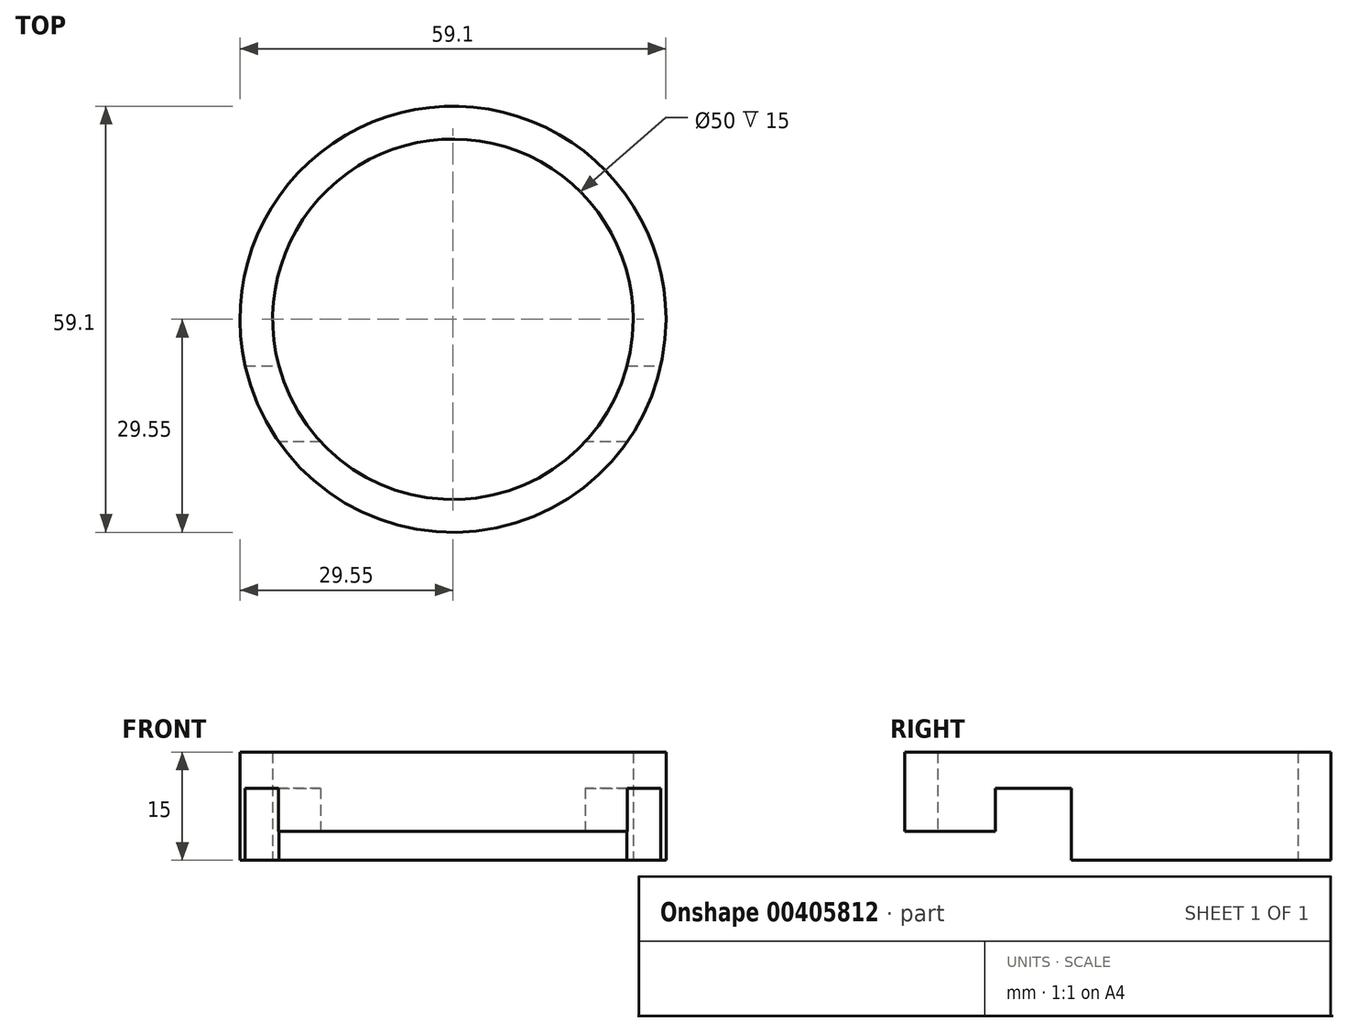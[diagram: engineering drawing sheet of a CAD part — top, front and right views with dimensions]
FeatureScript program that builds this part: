
annotation { "Feature Type Name" : "Feature", "Feature Type Description" : "" }
export const myFeature = defineFeature(function(context is Context, id is Id, definition is map)
    precondition{}
    {
        {
            var Q0;
            Q0=qCreatedBy(makeId("Top.planeOp"),FACE);
            var sketch = newSketch(context, id + "F0", { "sketchPlane" : qUnion([Q0])});
            skCircle(sketch, "E0", {"center": v(0, 0) * mm, "radius": 29.55 * mm});
            skCircle(sketch, "E1", {"center": v(0, 0) * mm, "radius": 25 * mm});
            skSolve(sketch);
        }
        {
            var Q0;
            Q0 = qSketchRegion(id + "F0", true);
            extrude(context, id + "F1", {"entities" : qUnion([Q0]), "depth" : 15 * mm});
        }
        {
            var Q0;
            Q0=qCreatedBy(makeId("Top.planeOp"),FACE);
            var sketch = newSketch(context, id + "F2", { "sketchPlane" : qUnion([Q0])});
            skLineSegment(sketch, "E2", {"start": v(-26.47, -10.46) * mm, "end": v(29.4, -10.46) * mm});
            skLineSegment(sketch, "E3", {"start": v(29.4, -10.46) * mm, "end": v(29.4, -17) * mm});
            skLineSegment(sketch, "E4", {"start": v(29.4, -17) * mm, "end": v(-27.45, -17) * mm});
            skLineSegment(sketch, "E5", {"start": v(-27.45, -17) * mm, "end": v(-26.47, -10.46) * mm});
            skSolve(sketch);
        }
        {
            var Q0;
            Q0 = qSketchRegion(id + "F2", true);
            extrude(context, id + "F3", {"entities" : qUnion([Q0]), "operationType" : NewBodyOperationType.REMOVE, "depth" : 10 * mm});
        }
        {
            var Q0;
            {var subQ0=sQuery(id+"F0.wireOp",EDGE,"E0");var subQ1=sQuery(id+"F0.wireOp",EDGE,"E1");Q0=makeQuery(id+"F3.boolean.opBoolean","SPLIT",FACE,{"disambiguationData":[TD([makeQuery(id+"F3.opExtrude","SWEPT_FACE",FACE,{"disambiguationData":[OSD([sQuery(id+"F2.wireOp",EDGE,"E4")])]})])],"derivedFrom":makeQuery(id+"F1.opExtrude","CAP_FACE",FACE,{"disambiguationData":[OSD([subQ0,subQ1])],"isStart":true})});}
            extrude(context, id + "F4", {"entities" : qUnion([Q0]), "operationType" : NewBodyOperationType.REMOVE, "oppositeDirection" : true, "depth" : 4 * mm});
        }
        {
            var Q0;
            Q0=makeQuery(id+"F3.boolean.opBoolean","COPY",FACE,{"derivedFrom":makeQuery(id+"F3.opExtrude","SWEPT_FACE",FACE,{"disambiguationData":[OSD([sQuery(id+"F2.wireOp",EDGE,"E5")])]})});
            extrude(context, id + "F5", {"entities" : qUnion([Q0]), "operationType" : NewBodyOperationType.REMOVE, "oppositeDirection" : true, "depth" : 25 * mm});
        }
        {
            var Q0;
            {var subQ0=sQuery(id+"F0.wireOp",EDGE,"E0");var subQ1=sQuery(id+"F2.wireOp",EDGE,"E2");Q0=makeQuery(id+"F3.boolean.opBoolean","COPY",FACE,{"disambiguationData":[TD([makeQuery(id+"F1.opExtrude","SWEPT_FACE",FACE,{"disambiguationData":[OSD([subQ0])]})])],"derivedFrom":makeQuery(id+"F3.opExtrude","SWEPT_FACE",FACE,{"disambiguationData":[OSD([subQ1])]})});}
            var Q1;
            {var subQ1=sQuery(id+"F2.wireOp",EDGE,"E5");var subQ2=sQuery(id+"F2.wireOp",EDGE,"E2");Q1=makeQuery(id+"F3.boolean.opBoolean","COPY",FACE,{"disambiguationData":[TD([makeQuery(id+"F3.opExtrude","SWEPT_FACE",FACE,{"disambiguationData":[OSD([subQ1])]})])],"derivedFrom":makeQuery(id+"F3.opExtrude","SWEPT_FACE",FACE,{"disambiguationData":[OSD([subQ2])]})});}
            extrude(context, id + "F6", {"entities" : qUnion([Q0, Q1]), "operationType" : NewBodyOperationType.REMOVE, "oppositeDirection" : true, "depth" : 4 * mm});
        }
        {
            var Q0;
            Q0=makeQuery(id+"F6.boolean.opBoolean","COPY",FACE,{"derivedFrom":makeQuery(id+"F6.opExtrude","SWEPT_FACE",FACE,{"disambiguationData":[OSD([sQuery(id+"F2.wireOp",EDGE,"E2"),sQuery(id+"F2.wireOp",EDGE,"E5")])]})});
            var Q1;
            Q1=makeQuery(id+"F6.boolean.opBoolean","COPY",FACE,{"derivedFrom":makeQuery(id+"F6.opExtrude","SWEPT_FACE",FACE,{"disambiguationData":[OSD([sQuery(id+"F0.wireOp",EDGE,"E0"),sQuery(id+"F2.wireOp",EDGE,"E2")])]})});
            extrude(context, id + "F7", {"entities" : qUnion([Q0, Q1]), "operationType" : NewBodyOperationType.REMOVE, "oppositeDirection" : true, "depth" : 25 * mm});
        }
        {
            var Q0;
            Q0=makeQuery(id+"F6.boolean.opBoolean","COPY",FACE,{"derivedFrom":makeQuery(id+"F6.opExtrude","SWEPT_FACE",FACE,{"disambiguationData":[OSD([sQuery(id+"F0.wireOp",EDGE,"E0"),sQuery(id+"F2.wireOp",EDGE,"E2")])]})});
            extrude(context, id + "F8", {"entities" : qUnion([Q0]), "operationType" : NewBodyOperationType.REMOVE, "oppositeDirection" : true, "depth" : 25 * mm});
        }
    });
